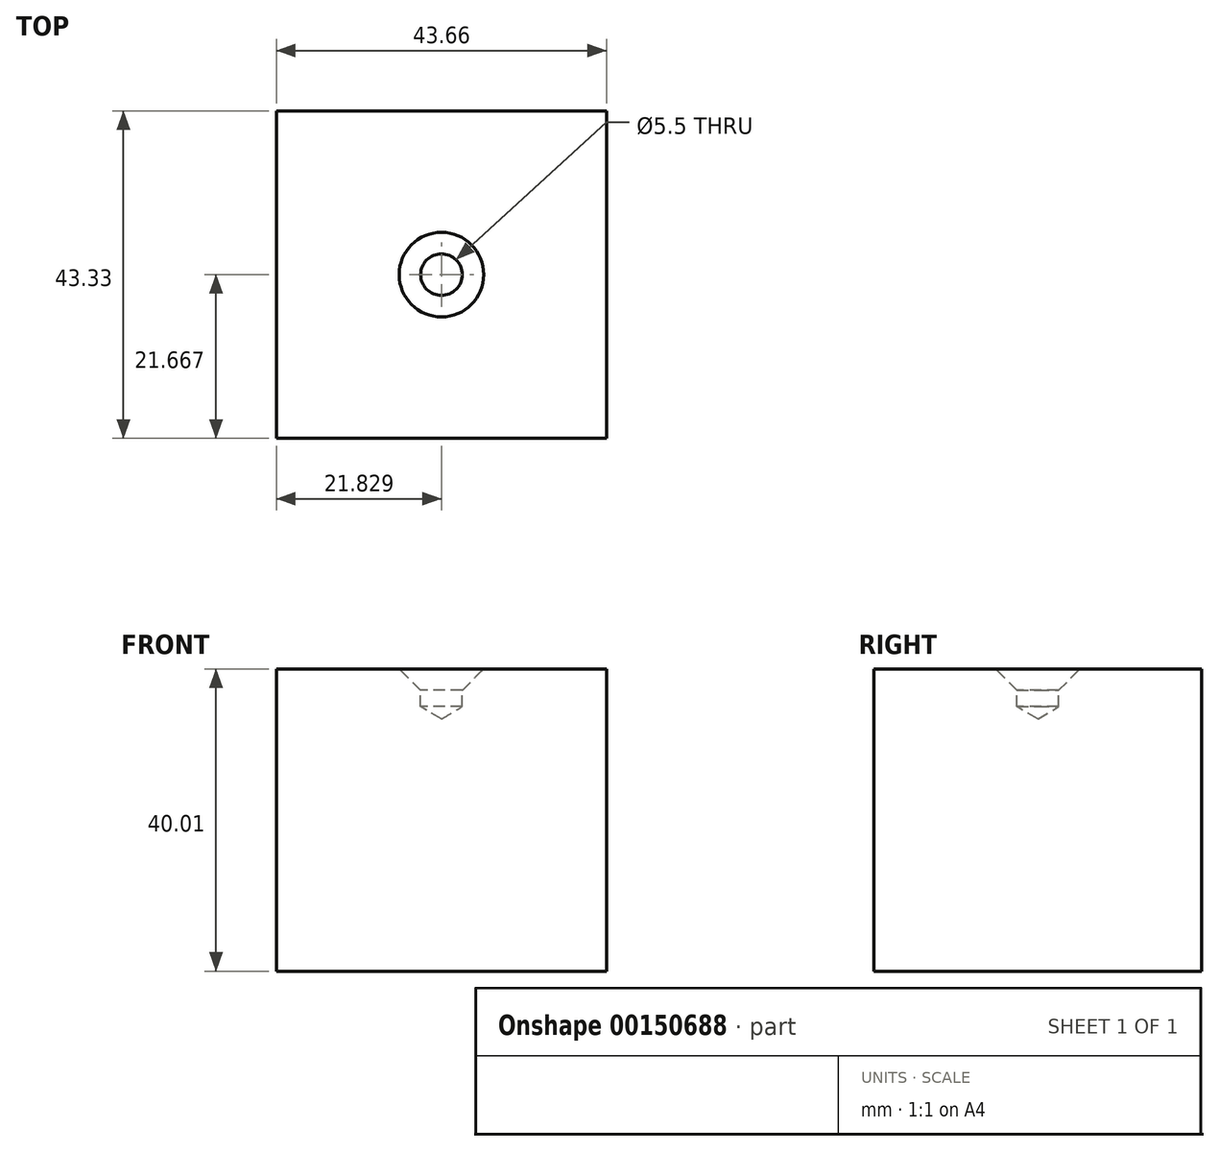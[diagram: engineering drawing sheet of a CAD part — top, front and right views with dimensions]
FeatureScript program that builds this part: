
annotation { "Feature Type Name" : "Feature", "Feature Type Description" : "" }
export const myFeature = defineFeature(function(context is Context, id is Id, definition is map)
    precondition{}
    {
        {
            var Q0;
            Q0=qCreatedBy(makeId("Top.planeOp"),FACE);
            var sketch = newSketch(context, id + "F0", { "sketchPlane" : qUnion([Q0])});
            skLineSegment(sketch, "E0.bottom", {"start": v(0, 0) * mm, "end": v(43.66, 0) * mm});
            skLineSegment(sketch, "E0.top", {"start": v(0, -43.33) * mm, "end": v(43.66, -43.33) * mm});
            skLineSegment(sketch, "E0.left", {"start": v(0, 0) * mm, "end": v(0, -43.33) * mm});
            skLineSegment(sketch, "E0.right", {"start": v(43.66, 0) * mm, "end": v(43.66, -43.33) * mm});
            skSolve(sketch);
        }
        {
            var Q0;
            Q0=makeQuery(id+"F0.imprint","IMPRINT",FACE,{"disambiguationData":[TD([[makeQuery(id+"F0.imprint","IMPRINT",EDGE,{"derivedFrom":sQuery(id+"F0.wireOp",EDGE,"E0.bottom")}),-1.0]])]});
            extrude(context, id + "F1", {"entities" : qUnion([Q0]), "depth" : 40 * mm});
        }
        {
            var Q0;
            Q0=makeQuery(id+"F1.opExtrude","CAP_FACE",FACE,{"disambiguationData":[OSD([sQuery(id+"F0.wireOp",EDGE,"E0.bottom"),sQuery(id+"F0.wireOp",EDGE,"E0.top"),sQuery(id+"F0.wireOp",EDGE,"E0.left"),sQuery(id+"F0.wireOp",EDGE,"E0.right")])],"isStart":false});
            var sketch = newSketch(context, id + "F2", { "sketchPlane" : qUnion([Q0])});
            skCircle(sketch, "E1", {"center": v(21.83, -21.66) * mm, "radius": 1.8 * mm});
            skSolve(sketch);
        }
        {
            var Q0;
            Q0=sQuery(id+"F2.wireOp",VERTEX,"E1.center");
            var Q1;
            Q1=makeQuery(id+"F1.opExtrude","SWEPT_BODY",BODY,{"disambiguationData":[OSD([sQuery(id+"F0.wireOp",EDGE,"E0.bottom"),sQuery(id+"F0.wireOp",EDGE,"E0.top"),sQuery(id+"F0.wireOp",EDGE,"E0.left"),sQuery(id+"F0.wireOp",EDGE,"E0.right")])]});
            hole(context, id + "F3", {"style" : HoleStyle.C_SINK, "endStyle" : HoleEndStyle.BLIND, "standardTappedOrClearance" : lookupTablePath({ "standard" : "ISO", "fit" : "Normal", "size" : "M5", "type" : "Clearance" }), "standardBlindInLast" : lookupTablePath({ "fit" : "Standard", "standard" : "ISO", "size" : "M5", "type" : "Clearance" }), "holeDiameter" : 5.5 * mm, "cSinkDiameter" : 11.2 * mm, "cSinkAngle" : 90 * degree, "holeDepth" : 5 * mm, "locations" : qUnion([Q0]), "scope" : qUnion([Q1])});
        }
    });
